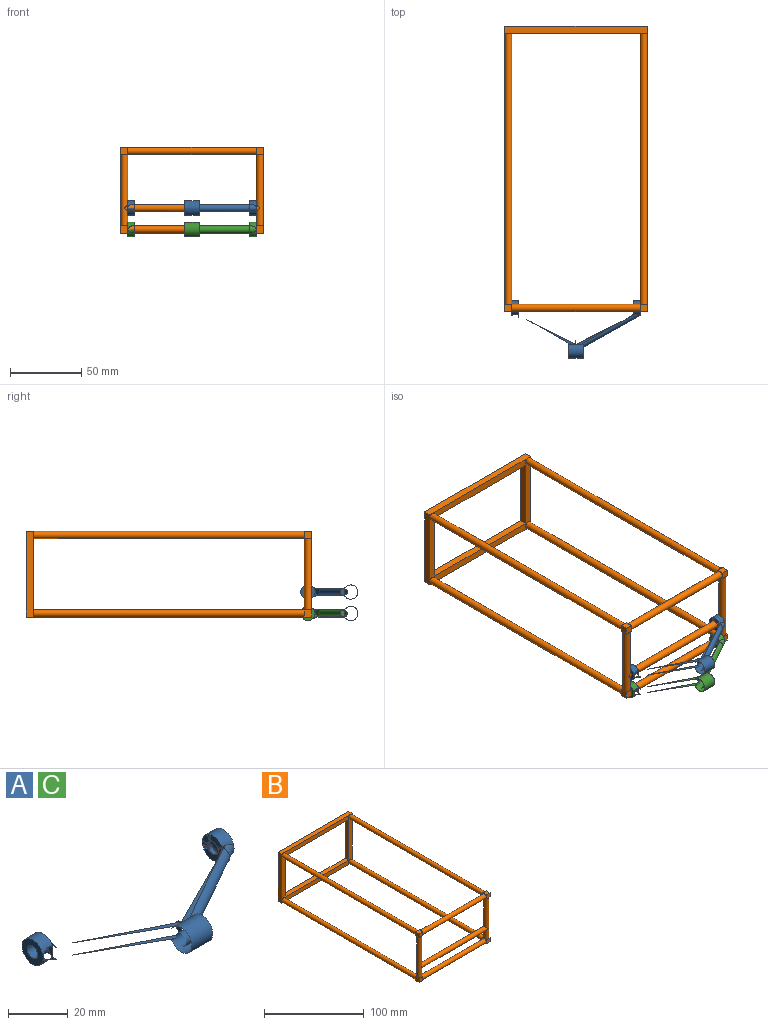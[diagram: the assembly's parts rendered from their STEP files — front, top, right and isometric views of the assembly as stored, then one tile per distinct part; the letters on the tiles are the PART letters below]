
ASSEMBLY  parts=3 mates=2
PART A: 18 faces, bbox 90x40x10 mm
  f0: plane 68.77x17.57mm, normal (0,0,1), area 68.3mm2, adj f11,f14,f15,f16,f17
  f1: plane 68.77x17.57mm, normal (0,0,-1), area 68.3mm2, adj f11,f14,f15,f16,f17
  f2: plane 10x10mm, normal (-1,0,0), area 58.9mm2, adj f4,f5
  f3: plane 10x10mm, normal (1,0,0), area 58.9mm2, adj f7,f8
  f4: cylinder r=2.5mm len=5mm, axis (-1,0,0), area 235.6mm2, adj f2,f6
  f5: cylinder r=5mm len=10mm, axis (-1,0,0), area 135mm2, adj f2,f6,f15,f16
  f6: plane 13.09x10mm, normal (1,0,0), area -32.8mm2, adj f4,f5,f16
  f7: cylinder r=2.5mm len=5mm, axis (1,0,0), area 235.6mm2, adj f3,f9
  f8: cylinder r=5mm len=10mm, axis (1,0,0), area 135mm2, adj f3,f9,f14,f17
  f9: plane 13.09x10mm, normal (-1,0,0), area -32.8mm2, adj f7,f8,f17
  f10: cylinder r=2.5mm len=10mm, axis (-1,0,0), area 471.2mm2, adj f12,f13
  f11: cylinder r=5mm len=10mm, axis (-1,0,0), area 262.4mm2, adj f0,f1,f12,f13,f14,f15
  f12: plane 13.24x10mm, normal (1,0,0), area -33.9mm2, adj f10,f11,f14
  f13: plane 13.24x10mm, normal (-1,0,0), area -33.9mm2, adj f10,f11,f15
  f14: cylinder r=2.5mm len=43.07mm, axis (0.87,0.49,0), area 282.8mm2, adj f0,f1,f8,f11,f12,f17
  f15: cylinder r=2.5mm len=43.07mm, axis (0.87,-0.49,0), area 1746.9mm2, adj f0,f1,f5,f11,f13,f16
  f16: cylinder r=2.5mm len=43.81mm, axis (-0.89,0.45,0), area 296.2mm2, adj f0,f1,f5,f6,f15,f17
  f17: cylinder r=2.5mm len=43.81mm, axis (-0.89,-0.45,0), area 296.2mm2, adj f0,f1,f8,f9,f14,f16
PART B: 83 faces, bbox 100x200x60 mm
  f0: cylinder r=2.5mm len=50mm, axis (0,0,1), area 760.4mm2, adj f66,f67,f72,f73,f74,f75,f76,f77
  f1: cylinder r=2.5mm len=50mm, axis (0,0,1), area 760.4mm2, adj f68,f69,f70,f71,f78,f79,f80,f81
  f2: plane 2.5x2.5mm, normal (0,1,0), area 1.3mm2, adj f37,f52,f81
  f3: plane 5x5mm, normal (1,0,0), area 25mm2, adj f14,f16,f25,f61,f70,f80
  f4: plane 2.5x2.5mm, normal (-1,0,0), area 1.3mm2, adj f14,f47,f78
  f5: plane 5x5mm, normal (0,-1,0), area 25mm2, adj f13,f26,f37,f45,f71,f79
  f6: plane 5x5mm, normal (-1,0,0), area 25mm2, adj f7,f18,f20,f65,f66,f76
  f7: plane 5x5mm, normal (0,-1,0), area 25mm2, adj f6,f20,f27,f49,f72,f76
  f8: plane 2.5x2.5mm, normal (1,0,0), area 1.3mm2, adj f42,f44,f75
  f9: plane 2.5x2.5mm, normal (0,1,0), area 1.3mm2, adj f11,f51,f74
  f10: plane 2.5x2.5mm, normal (1,0,0), area 1.3mm2, adj f32,f44,f73
  f11: plane 2.5x2.5mm, normal (1,0,0), area 1.3mm2, adj f9,f47,f74
  f12: plane 2.5x2.5mm, normal (-1,0,0), area 1.3mm2, adj f41,f47,f68
  f13: plane 2.5x2.5mm, normal (-1,0,0), area 1.3mm2, adj f5,f44,f79
  f14: plane 5x5mm, normal (0,-1,0), area 25mm2, adj f3,f4,f25,f48,f70,f78
  f15: plane 2.5x2.5mm, normal (0,1,0), area 1.3mm2, adj f29,f52,f69
  f16: plane 2.5x2.5mm, normal (0,1,0), area 1.3mm2, adj f3,f56,f80
  f17: plane 2.5x2.5mm, normal (0,1,0), area 1.3mm2, adj f19,f50,f67
  f18: plane 2.5x2.5mm, normal (0,1,0), area 1.3mm2, adj f6,f51,f66
  f19: plane 5x5mm, normal (-1,0,0), area 25mm2, adj f17,f21,f32,f59,f67,f77
  f20: plane 5x5mm, normal (0,0,-1), area 25mm2, adj f6,f7,f35,f49,f55,f65
  f21: plane 5x5mm, normal (0,0,1), area 25mm2, adj f19,f22,f32,f46,f59,f63
  f22: plane 2.5x2.5mm, normal (1,0,0), area 1.3mm2, adj f21,f44,f63
  f23: plane 60x5mm, normal (1,0,0), area 300mm2, adj f24,f31,f38,f43,f53,f60
  f24: plane 100x5mm, normal (0,0,1), area 500mm2, adj f23,f30,f38,f43,f53,f58
  f25: plane 5x5mm, normal (0,0,-1), area 25mm2, adj f3,f14,f28,f48,f57,f61
  f26: plane 5x5mm, normal (0,0,1), area 25mm2, adj f5,f36,f37,f45,f54,f62
  f27: plane 2.5x2.5mm, normal (1,0,0), area 1.3mm2, adj f7,f47,f72
  f28: plane 2.5x2.5mm, normal (-1,0,0), area 1.3mm2, adj f25,f47,f57
  f29: plane 2.5x2.5mm, normal (-1,0,0), area 1.3mm2, adj f15,f44,f69
  f30: plane 60x5mm, normal (-1,0,0), area 300mm2, adj f24,f31,f38,f43,f58,f64
  f31: plane 100x5mm, normal (0,0,-1), area 500mm2, adj f23,f30,f38,f43,f60,f64
  f32: plane 5x5mm, normal (0,-1,0), area 25mm2, adj f10,f19,f21,f46,f73,f77
  f33: plane 90x5mm, normal (0,0,1), area 450mm2, adj f38,f39,f40,f43
  f34: plane 90x5mm, normal (0,0,-1), area 450mm2, adj f38,f39,f40,f43
  f35: plane 2.5x2.5mm, normal (1,0,0), area 1.3mm2, adj f20,f47,f55
  f36: plane 2.5x2.5mm, normal (-1,0,0), area 1.3mm2, adj f26,f44,f62
  f37: plane 5x5mm, normal (1,0,0), area 25mm2, adj f2,f5,f26,f54,f71,f81
  f38: plane 100x60mm, normal (0,1,0), area 1500mm2, adj f23,f24,f30,f31,f33,f34,f39,f40
  f39: plane 50x5mm, normal (1,0,0), area 250mm2, adj f33,f34,f38,f43
  f40: plane 50x5mm, normal (-1,0,0), area 250mm2, adj f33,f34,f38,f43
  f41: plane 2.5x2.5mm, normal (0,1,0), area 1.3mm2, adj f12,f56,f68
  f42: plane 2.5x2.5mm, normal (0,1,0), area 1.3mm2, adj f8,f50,f75
  f43: plane 100x60mm, normal (0,-1,0), area 1416.1mm2, adj f23,f24,f30,f31,f33,f34,f39,f40
  f44: cylinder r=2.5mm len=90mm, axis (-1,0,0), area 1413.7mm2, adj f8,f10,f13,f22,f29,f36,f45,f46
  f45: plane 2.5x2.5mm, normal (-1,0,0), area 1.3mm2, adj f5,f26,f44
  f46: plane 2.5x2.5mm, normal (1,0,0), area 1.3mm2, adj f21,f32,f44
  f47: cylinder r=2.5mm len=90mm, axis (-1,0,0), area 1413.7mm2, adj f4,f11,f12,f27,f28,f35,f48,f49
  f48: plane 2.5x2.5mm, normal (-1,0,0), area 1.3mm2, adj f14,f25,f47
  f49: plane 2.5x2.5mm, normal (1,0,0), area 1.3mm2, adj f7,f20,f47
  f50: cylinder r=2.5mm len=190mm, axis (0,-1,0), area 2984.5mm2, adj f17,f42,f43,f58,f59,f63
  f51: cylinder r=2.5mm len=190mm, axis (0,-1,0), area 2984.5mm2, adj f9,f18,f43,f55,f64,f65
  f52: cylinder r=2.5mm len=190mm, axis (0,-1,0), area 2984.5mm2, adj f2,f15,f43,f53,f54,f62
  f53: plane 2.5x2.5mm, normal (0,-1,0), area 1.3mm2, adj f23,f24,f52
  f54: plane 2.5x2.5mm, normal (0,1,0), area 1.3mm2, adj f26,f37,f52
  f55: plane 2.5x2.5mm, normal (0,1,0), area 1.3mm2, adj f20,f35,f51
  f56: cylinder r=2.5mm len=190mm, axis (0,-1,0), area 2984.5mm2, adj f16,f41,f43,f57,f60,f61
  f57: plane 2.5x2.5mm, normal (0,1,0), area 1.3mm2, adj f25,f28,f56
  f58: plane 2.5x2.5mm, normal (0,-1,0), area 1.3mm2, adj f24,f30,f50
  f59: plane 2.5x2.5mm, normal (0,1,0), area 1.3mm2, adj f19,f21,f50
  f60: plane 2.5x2.5mm, normal (0,-1,0), area 1.3mm2, adj f23,f31,f56
  f61: plane 2.5x2.5mm, normal (0,1,0), area 1.3mm2, adj f3,f25,f56
  f62: plane 2.5x2.5mm, normal (0,1,0), area 1.3mm2, adj f26,f36,f52
  f63: plane 2.5x2.5mm, normal (0,1,0), area 1.3mm2, adj f21,f22,f50
  f64: plane 2.5x2.5mm, normal (0,-1,0), area 1.3mm2, adj f30,f31,f51
  f65: plane 2.5x2.5mm, normal (0,1,0), area 1.3mm2, adj f6,f20,f51
  f66: plane 2.5x2.5mm, normal (0,0,1), area 1.3mm2, adj f0,f6,f18
  f67: plane 2.5x2.5mm, normal (0,0,-1), area 1.3mm2, adj f0,f17,f19
  f68: plane 2.5x2.5mm, normal (0,0,1), area 1.3mm2, adj f1,f12,f41
  f69: plane 2.5x2.5mm, normal (0,0,-1), area 1.3mm2, adj f1,f15,f29
  f70: plane 2.5x2.5mm, normal (0,0,1), area 1.3mm2, adj f1,f3,f14
  f71: plane 2.5x2.5mm, normal (0,0,-1), area 1.3mm2, adj f1,f5,f37
  f72: plane 2.5x2.5mm, normal (0,0,1), area 1.3mm2, adj f0,f7,f27
  f73: plane 2.5x2.5mm, normal (0,0,-1), area 1.3mm2, adj f0,f10,f32
  f74: plane 2.5x2.5mm, normal (0,0,1), area 1.3mm2, adj f0,f9,f11
  f75: plane 2.5x2.5mm, normal (0,0,-1), area 1.3mm2, adj f0,f8,f42
  f76: plane 2.5x2.5mm, normal (0,0,1), area 1.3mm2, adj f0,f6,f7
  f77: plane 2.5x2.5mm, normal (0,0,-1), area 1.3mm2, adj f0,f19,f32
  f78: plane 2.5x2.5mm, normal (0,0,1), area 1.3mm2, adj f1,f4,f14
  f79: plane 2.5x2.5mm, normal (0,0,-1), area 1.3mm2, adj f1,f5,f13
  f80: plane 2.5x2.5mm, normal (0,0,1), area 1.3mm2, adj f1,f3,f16
  f81: plane 2.5x2.5mm, normal (0,0,-1), area 1.3mm2, adj f1,f2,f37
  f82: cylinder r=2.5mm len=95mm, axis (-1,0,0), area 1442.3mm2, adj f0,f1
PART C: same geometry as A
PLACE A t=(-36.3,-31.73,14.34)mm
PLACE B t=(-63.15,-31.73,-15.85)mm
PLACE C t=(-36.3,-31.73,-0.66)mm
MATE planar A.f4 <-> B.f44  axis (-1,0,0) through (-58.15,-29.23,1.65)mm
MATE planar C.f4 <-> B.f47  axis (-1,0,0) through (-58.15,-29.23,-13.35)mm
